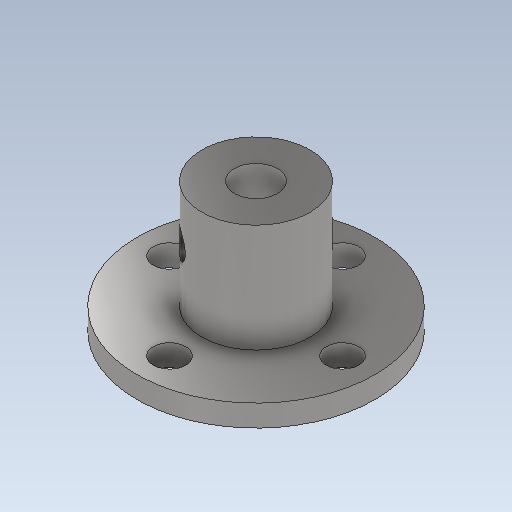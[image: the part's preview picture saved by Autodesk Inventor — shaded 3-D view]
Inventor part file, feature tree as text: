
AUTODESK INVENTOR PART (.ipt)
format: ipt  version: 2020.2 (Build 242310000, 310)  size: 217,088 bytes
history: native  units: mm
features: sketch x7, extrude x5, hole x2
ambient origin geometry x8: Origin, YZ Plane, XZ Plane, XY Plane, X Axis, Y Axis, Z Axis, Center Point
bodies: Solido1 (feature_tree)
feature tree (14):
  extrude  "Estrusione1"  Depth=22.0mm
  extrude  "Estrusione2"  Depth=2.0mm TaperAngle=0.0deg
  extrude  "Estrusione3"  Depth=10.0mm
  extrude  "Estrusione4"  Depth=10.0mm TaperAngle=0.0deg
  hole  "Foro1"  [1 undecoded]
  sketch  "Schizzo7"
  hole  "Foro2"  [1 undecoded]
  extrude  "Estrusione5"  Depth=16.0mm
  sketch  "Schizzo1"
  sketch  "Schizzo2"
  sketch  "Schizzo3"
  sketch  "Schizzo4"
  sketch  "Schizzo5"
  sketch  "Schizzo6"
note: 2 required parameter values undecoded (feature->parameter linkage not recoverable at this tier; creation-order binding heuristic only, values carry confidence <= 0.55)
